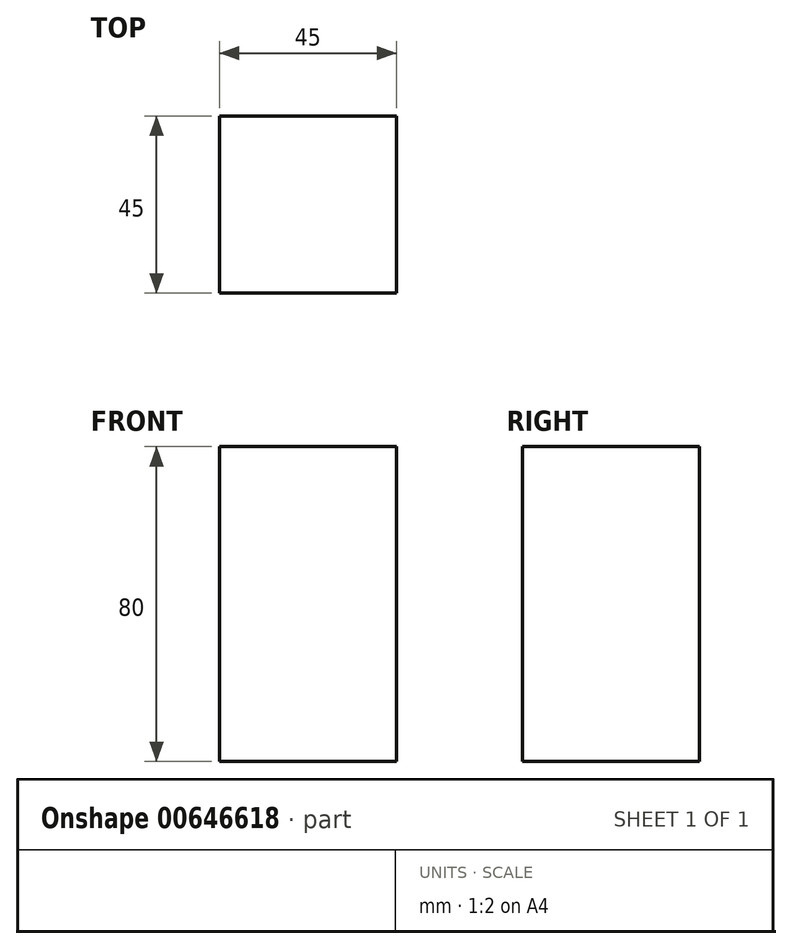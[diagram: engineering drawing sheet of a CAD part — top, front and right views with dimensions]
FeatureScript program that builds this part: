
annotation { "Feature Type Name" : "Feature", "Feature Type Description" : "" }
export const myFeature = defineFeature(function(context is Context, id is Id, definition is map)
    precondition{}
    {
        {
            var Q0;
            Q0=qCreatedBy(makeId("Top.planeOp"),FACE);
            var sketch = newSketch(context, id + "F0", { "sketchPlane" : qUnion([Q0])});
            skLineSegment(sketch, "E0.bottom", {"start": v(0, 0) * mm, "end": v(45, 0) * mm});
            skLineSegment(sketch, "E0.top", {"start": v(0, 45) * mm, "end": v(45, 45) * mm});
            skLineSegment(sketch, "E0.left", {"start": v(0, 0) * mm, "end": v(0, 45) * mm});
            skLineSegment(sketch, "E0.right", {"start": v(45, 0) * mm, "end": v(45, 45) * mm});
            skSolve(sketch);
        }
        {
            var Q0;
            Q0 = qSketchRegion(id + "F0", true);
            extrude(context, id + "F1", {"entities" : qUnion([Q0]), "depth" : 80 * mm, "offsetDistance" : 25 * mm});
        }
    });
